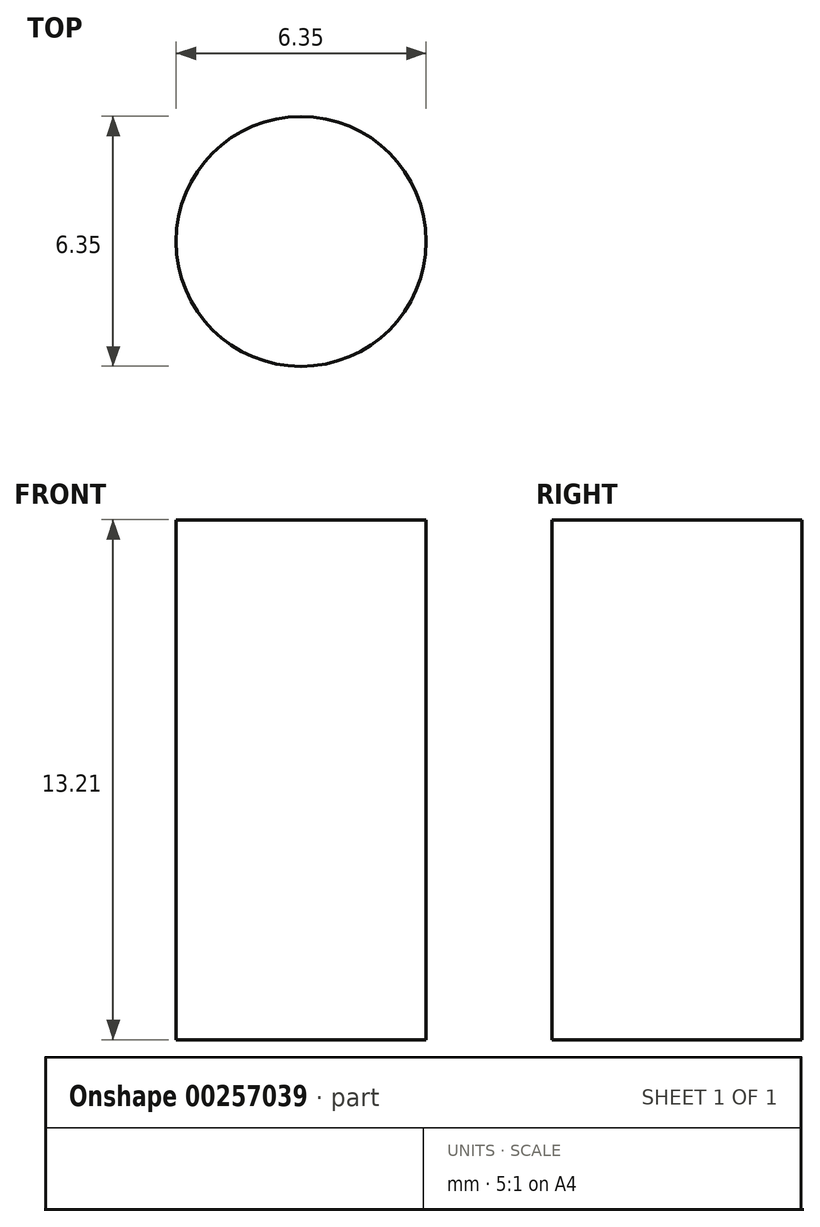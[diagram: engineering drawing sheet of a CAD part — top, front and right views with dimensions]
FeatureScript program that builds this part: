
annotation { "Feature Type Name" : "Feature", "Feature Type Description" : "" }
export const myFeature = defineFeature(function(context is Context, id is Id, definition is map)
    precondition{}
    {
        {
            var Q0;
            Q0=qCreatedBy(makeId("Top.planeOp"),FACE);
            var sketch = newSketch(context, id + "F0", { "sketchPlane" : qUnion([Q0])});
            skCircle(sketch, "E0", {"center": v(-35.02, 9.44) * mm, "radius": 3.18 * mm});
            skSolve(sketch);
        }
        {
            var Q0;
            Q0 = qSketchRegion(id + "F0", true);
            extrude(context, id + "F1", {"entities" : qUnion([Q0]), "depth" : 13.2 * mm});
        }
    });
